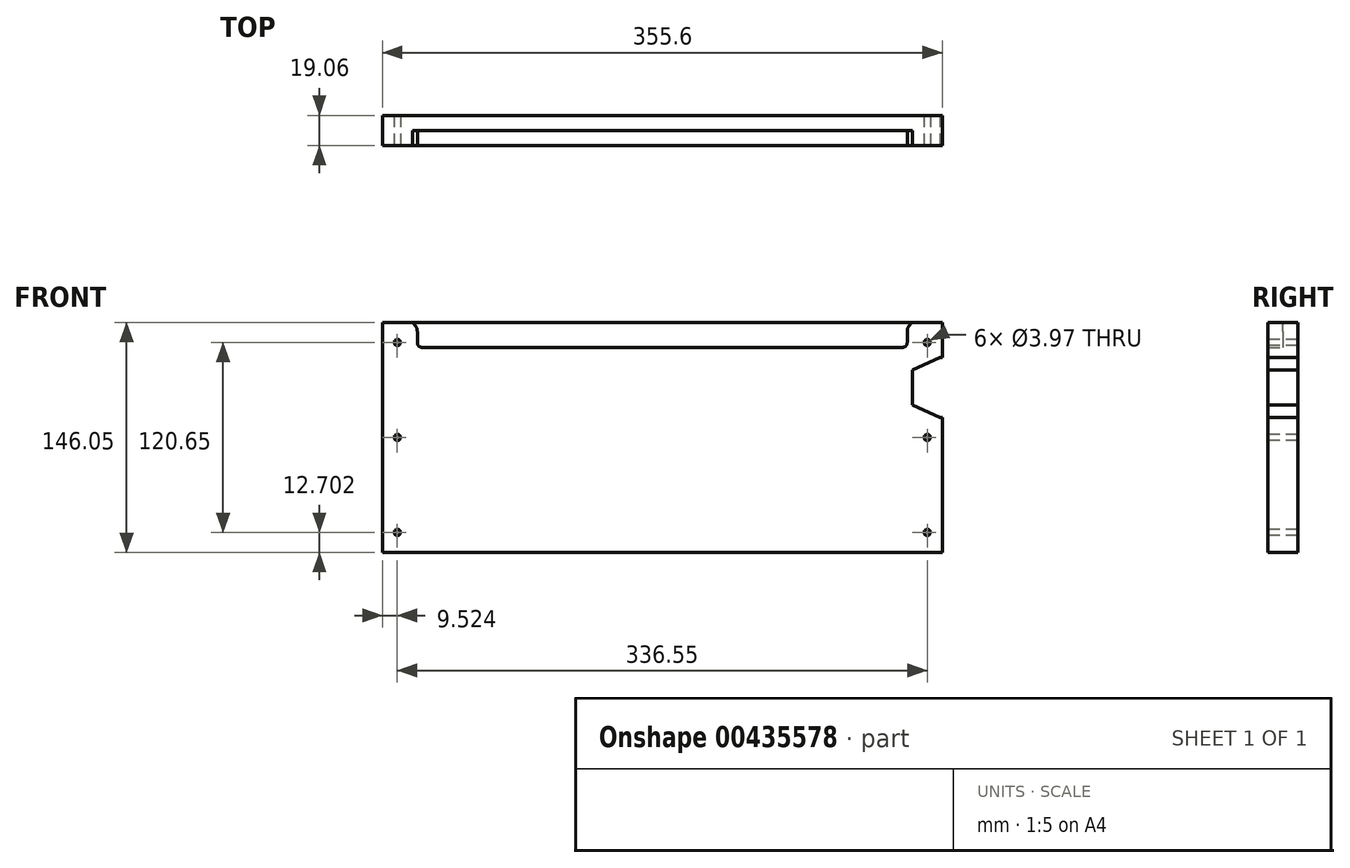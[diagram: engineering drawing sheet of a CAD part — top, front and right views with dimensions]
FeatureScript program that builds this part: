
annotation { "Feature Type Name" : "Feature", "Feature Type Description" : "" }
export const myFeature = defineFeature(function(context is Context, id is Id, definition is map)
    precondition{}
    {
        {
            var Q0;
            Q0=qCreatedBy(makeId("Front.planeOp"),FACE);
            var sketch = newSketch(context, id + "F0", { "sketchPlane" : qUnion([Q0])});
            skLineSegment(sketch, "E0", {"start": v(109.86, 42.77) * mm, "end": v(109.86, 55.47) * mm});
            skLineSegment(sketch, "E1", {"start": v(-198.11, 39.6) * mm, "end": v(106.69, 39.6) * mm});
            skLineSegment(sketch, "E2.bottom", {"start": v(-223.51, 55.47) * mm, "end": v(132.09, 55.47) * mm});
            skLineSegment(sketch, "E2.top", {"start": v(-223.51, -90.58) * mm, "end": v(132.09, -90.58) * mm});
            skLineSegment(sketch, "E2.right", {"start": v(132.09, 55.47) * mm, "end": v(132.09, -90.58) * mm});
            skLineSegment(sketch, "E3", {"start": v(-223.51, -17.55) * mm, "end": v(132.09, -17.55) * mm, "construction": true});
            skLineSegment(sketch, "E4", {"start": v(-45.71, 55.47) * mm, "end": v(-45.71, -90.58) * mm, "construction": true});
            skLineSegment(sketch, "E5", {"start": v(132.09, -30.25) * mm, "end": v(131.88, -30.25) * mm});
            skLineSegment(sketch, "E6", {"start": v(129.25, -30.82) * mm, "end": v(116.76, -36.5) * mm});
            skLineSegment(sketch, "E7", {"start": v(113.04, -42.28) * mm, "end": v(113.04, -56.33) * mm});
            skLineSegment(sketch, "E8", {"start": v(116.76, -62.1) * mm, "end": v(129.25, -67.78) * mm});
            skLineSegment(sketch, "E9", {"start": v(131.88, -68.35) * mm, "end": v(132.09, -68.35) * mm});
            skPoint(sketch, "E10.visualSharp", {"position": v(130.5, -30.25) * mm});
            skArc(sketch, "E10.filletArc", {"start": v(131.88, -30.25) * mm, "mid": v(130.53, -30.4) * mm, "end": v(129.25, -30.82) * mm});
            skPoint(sketch, "E11.visualSharp", {"position": v(113.04, -38.2) * mm});
            skArc(sketch, "E11.filletArc", {"start": v(116.76, -36.5) * mm, "mid": v(114.05, -38.84) * mm, "end": v(113.04, -42.28) * mm});
            skPoint(sketch, "E12.visualSharp", {"position": v(113.04, -60.42) * mm});
            skArc(sketch, "E12.filletArc", {"start": v(113.04, -56.33) * mm, "mid": v(114.05, -59.76) * mm, "end": v(116.76, -62.1) * mm});
            skPoint(sketch, "E13.visualSharp", {"position": v(130.5, -68.35) * mm});
            skArc(sketch, "E13.filletArc", {"start": v(129.25, -67.78) * mm, "mid": v(130.53, -68.2) * mm, "end": v(131.88, -68.35) * mm});
            skLineSegment(sketch, "E14.MirrorCS", {"start": v(-223.51, 55.47) * mm, "end": v(-223.51, -90.58) * mm});
            skArc(sketch, "E15.filletArc", {"start": v(-201.29, 42.77) * mm, "mid": v(-200.36, 40.53) * mm, "end": v(-198.11, 39.6) * mm});
            skArc(sketch, "E16.filletArc", {"start": v(106.69, 39.6) * mm, "mid": v(108.93, 40.53) * mm, "end": v(109.86, 42.77) * mm});
            skLineSegment(sketch, "E17.MirrorCS", {"start": v(131.88, 33.25) * mm, "end": v(132.09, 33.25) * mm});
            skLineSegment(sketch, "E18.MirrorCS", {"start": v(132.09, -4.85) * mm, "end": v(131.88, -4.85) * mm});
            skArc(sketch, "E19.MirrorCS", {"start": v(129.25, 32.68) * mm, "mid": v(130.53, 33.1) * mm, "end": v(131.88, 33.25) * mm});
            skArc(sketch, "E20.MirrorCS", {"start": v(131.88, -4.85) * mm, "mid": v(130.53, -4.7) * mm, "end": v(129.25, -4.28) * mm});
            skArc(sketch, "E21.MirrorCS", {"start": v(113.04, 21.22) * mm, "mid": v(114.05, 24.66) * mm, "end": v(116.76, 27) * mm});
            skLineSegment(sketch, "E22.MirrorCS", {"start": v(106.65, 22.4) * mm, "end": v(138.44, 36.85) * mm});
            skLineSegment(sketch, "E23.MirrorCS", {"start": v(138.44, -8.46) * mm, "end": v(106.65, 5.99) * mm});
            skLineSegment(sketch, "E24.MirrorCS", {"start": v(138.44, -4.85) * mm, "end": v(122.56, -4.85) * mm});
            skLineSegment(sketch, "E25.MirrorCS", {"start": v(122.56, 33.25) * mm, "end": v(138.44, 33.25) * mm});
            skArc(sketch, "E26.MirrorCS", {"start": v(116.76, 1.4) * mm, "mid": v(114.05, 3.74) * mm, "end": v(113.04, 7.17) * mm});
            skLineSegment(sketch, "E27.MirrorCS", {"start": v(129.25, -4.28) * mm, "end": v(116.76, 1.4) * mm});
            skLineSegment(sketch, "E28.MirrorCS", {"start": v(113.04, 7.17) * mm, "end": v(113.04, 21.22) * mm});
            skLineSegment(sketch, "E29.MirrorCS", {"start": v(116.76, 27) * mm, "end": v(129.25, 32.68) * mm});
            skLineSegment(sketch, "E30.MirrorCS", {"start": v(113.04, -1.68) * mm, "end": v(113.04, 36.42) * mm});
            skPoint(sketch, "E31.MirrorP", {"position": v(130.5, -4.85) * mm});
            skPoint(sketch, "E32.MirrorP", {"position": v(113.04, 25.3) * mm});
            skPoint(sketch, "E33.MirrorP", {"position": v(113.04, 3.08) * mm});
            skPoint(sketch, "E34.MirrorP", {"position": v(130.5, 33.25) * mm});
            skLineSegment(sketch, "E35.MirrorCS", {"start": v(-223.3, 33.25) * mm, "end": v(-223.51, 33.25) * mm});
            skLineSegment(sketch, "E36.MirrorCS", {"start": v(-223.51, -4.85) * mm, "end": v(-223.3, -4.85) * mm});
            skLineSegment(sketch, "E37.MirrorCS", {"start": v(-223.3, -68.35) * mm, "end": v(-223.51, -68.35) * mm});
            skArc(sketch, "E38.MirrorCS", {"start": v(-223.3, -30.25) * mm, "mid": v(-221.95, -30.4) * mm, "end": v(-220.67, -30.82) * mm});
            skArc(sketch, "E39.MirrorCS", {"start": v(-220.67, 32.68) * mm, "mid": v(-221.95, 33.1) * mm, "end": v(-223.3, 33.25) * mm});
            skArc(sketch, "E40.MirrorCS", {"start": v(-223.3, -4.85) * mm, "mid": v(-221.95, -4.7) * mm, "end": v(-220.67, -4.28) * mm});
            skArc(sketch, "E41.MirrorCS", {"start": v(-220.67, -67.78) * mm, "mid": v(-221.95, -68.2) * mm, "end": v(-223.3, -68.35) * mm});
            skLineSegment(sketch, "E42.MirrorCS", {"start": v(-223.51, -30.25) * mm, "end": v(-223.3, -30.25) * mm});
            skArc(sketch, "E43.MirrorCS", {"start": v(-208.18, -36.5) * mm, "mid": v(-205.47, -38.84) * mm, "end": v(-204.46, -42.28) * mm});
            skLineSegment(sketch, "E44.MirrorCS", {"start": v(-220.67, -4.28) * mm, "end": v(-208.18, 1.4) * mm});
            skArc(sketch, "E45.MirrorCS", {"start": v(-208.18, 1.4) * mm, "mid": v(-205.47, 3.74) * mm, "end": v(-204.46, 7.17) * mm});
            skArc(sketch, "E46.MirrorCS", {"start": v(-204.46, -56.33) * mm, "mid": v(-205.47, -59.76) * mm, "end": v(-208.18, -62.1) * mm});
            skArc(sketch, "E47.MirrorCS", {"start": v(-204.46, 21.22) * mm, "mid": v(-205.47, 24.66) * mm, "end": v(-208.18, 27) * mm});
            skLineSegment(sketch, "E48.MirrorCS", {"start": v(-220.67, -30.82) * mm, "end": v(-208.18, -36.5) * mm});
            skLineSegment(sketch, "E49.MirrorCS", {"start": v(-208.18, 27) * mm, "end": v(-220.67, 32.68) * mm});
            skLineSegment(sketch, "E50.MirrorCS", {"start": v(-208.18, -62.1) * mm, "end": v(-220.67, -67.78) * mm});
            skPoint(sketch, "E51.MirrorP", {"position": v(-204.46, 3.08) * mm});
            skPoint(sketch, "E52.MirrorP", {"position": v(-204.46, -38.2) * mm});
            skPoint(sketch, "E53.MirrorP", {"position": v(-221.92, 33.25) * mm});
            skPoint(sketch, "E54.MirrorP", {"position": v(-204.46, 25.3) * mm});
            skLineSegment(sketch, "E55.MirrorCS", {"start": v(-204.46, 7.17) * mm, "end": v(-204.46, 21.22) * mm});
            skPoint(sketch, "E56.MirrorP", {"position": v(-221.92, -68.35) * mm});
            skPoint(sketch, "E57.MirrorP", {"position": v(-204.46, -60.42) * mm});
            skLineSegment(sketch, "E58.MirrorCS", {"start": v(-204.46, -42.28) * mm, "end": v(-204.46, -56.33) * mm});
            skPoint(sketch, "E59.MirrorP", {"position": v(-221.92, -30.25) * mm});
            skPoint(sketch, "E60.MirrorP", {"position": v(-221.92, -4.85) * mm});
            skCircle(sketch, "E61", {"center": v(122.56, -77.88) * mm, "radius": 1.98 * mm});
            skCircle(sketch, "E62", {"center": v(122.56, -17.55) * mm, "radius": 1.98 * mm});
            skCircle(sketch, "E63.MirrorC", {"center": v(122.56, 42.77) * mm, "radius": 1.98 * mm});
            skCircle(sketch, "E64.MirrorC", {"center": v(-213.99, -77.88) * mm, "radius": 1.98 * mm});
            skCircle(sketch, "E65.MirrorC", {"center": v(-213.99, -17.55) * mm, "radius": 1.98 * mm});
            skCircle(sketch, "E66.MirrorC", {"center": v(-213.99, 42.77) * mm, "radius": 1.98 * mm});
            skLineSegment(sketch, "E67", {"start": v(-201.29, 55.47) * mm, "end": v(-201.29, 42.77) * mm});
            skSolve(sketch);
        }
        {
            var Q0;
            {var subQ22=sQuery(id+"F0.wireOp",EDGE,"E0");Q0=makeQuery(id+"F0.imprint","IMPRINT",FACE,{"disambiguationData":[TD([[makeQuery(id+"F0.imprint","IMPRINT",EDGE,{"derivedFrom":subQ22}),-1.0]])]});}
            var Q1;
            {var subQ1=sQuery(id+"F0.wireOp",EDGE,"E0");Q1=makeQuery(id+"F0.imprint","IMPRINT",FACE,{"disambiguationData":[TD([[makeQuery(id+"F0.imprint","IMPRINT",EDGE,{"derivedFrom":subQ1}),1.0]])]});}
            var Q2;
            {var subQ0=sQuery(id+"F0.wireOp",EDGE,"E24.MirrorCS");var subQ1=sQuery(id+"F0.wireOp",EDGE,"E2.right");var subQ2=makeQuery(id+"F0.imprint","INTERSECT",VERTEX,{"derivedFrom":[subQ1,subQ0]});Q2=makeQuery(id+"F0.imprint","IMPRINT",FACE,{"disambiguationData":[TD([[makeQuery(id+"F0.imprint","IMPRINT",EDGE,{"disambiguationData":[TD([[subQ2,-1.0]])],"derivedFrom":subQ1}),-1.0]])]});}
            var Q3;
            {var subQ0=sQuery(id+"F0.wireOp",EDGE,"E22.MirrorCS");var subQ1=sQuery(id+"F0.wireOp",EDGE,"E2.right");var subQ2=makeQuery(id+"F0.imprint","INTERSECT",VERTEX,{"derivedFrom":[subQ1,subQ0]});Q3=makeQuery(id+"F0.imprint","IMPRINT",FACE,{"disambiguationData":[TD([[makeQuery(id+"F0.imprint","IMPRINT",EDGE,{"disambiguationData":[TD([[subQ2,-1.0]])],"derivedFrom":subQ1}),-1.0]])]});}
            extrude(context, id + "F1", {"entities" : qUnion([Q0, Q1, Q2, Q3]), "oppositeDirection" : true, "depth" : 9.52 * mm, "offsetDistance" : 25.4 * mm});
        }
        {
            var Q0;
            {var subQ22=sQuery(id+"F0.wireOp",EDGE,"E0");Q0=makeQuery(id+"F0.imprint","IMPRINT",FACE,{"disambiguationData":[TD([[makeQuery(id+"F0.imprint","IMPRINT",EDGE,{"derivedFrom":subQ22}),-1.0]])]});}
            var Q1;
            {var subQ0=sQuery(id+"F0.wireOp",EDGE,"E22.MirrorCS");var subQ1=sQuery(id+"F0.wireOp",EDGE,"E2.right");var subQ2=makeQuery(id+"F0.imprint","INTERSECT",VERTEX,{"derivedFrom":[subQ1,subQ0]});Q1=makeQuery(id+"F0.imprint","IMPRINT",FACE,{"disambiguationData":[TD([[makeQuery(id+"F0.imprint","IMPRINT",EDGE,{"disambiguationData":[TD([[subQ2,-1.0]])],"derivedFrom":subQ1}),-1.0]])]});}
            var Q2;
            {var subQ0=sQuery(id+"F0.wireOp",EDGE,"E24.MirrorCS");var subQ1=sQuery(id+"F0.wireOp",EDGE,"E2.right");var subQ2=makeQuery(id+"F0.imprint","INTERSECT",VERTEX,{"derivedFrom":[subQ1,subQ0]});Q2=makeQuery(id+"F0.imprint","IMPRINT",FACE,{"disambiguationData":[TD([[makeQuery(id+"F0.imprint","IMPRINT",EDGE,{"disambiguationData":[TD([[subQ2,-1.0]])],"derivedFrom":subQ1}),-1.0]])]});}
            extrude(context, id + "F2", {"entities" : qUnion([Q0, Q1, Q2]), "operationType" : NewBodyOperationType.ADD, "depth" : 9.52 * mm, "offsetDistance" : 25.4 * mm});
        }
        {
            var Q0;
            Q0=makeQuery(id+"F2.opExtrude","SWEPT_EDGE",EDGE,{"disambiguationData":[OSD([sQuery(id+"F0.wireOp",EDGE,"E2.bottom"),sQuery(id+"F0.wireOp",EDGE,"E67")])]});
            var Q1;
            Q1=makeQuery(id+"F2.opExtrude","SWEPT_EDGE",EDGE,{"disambiguationData":[OSD([sQuery(id+"F0.wireOp",EDGE,"E0"),sQuery(id+"F0.wireOp",EDGE,"E2.bottom")])]});
            chamfer(context, id + "F3", {"entities" : qUnion([Q0, Q1]), "width" : 3.17 * mm, "tangentPropagation" : true});
        }
        {
            var Q0;
            {var subQ0=sQuery(id+"F0.wireOp",EDGE,"E0");Q0=makeQuery(id+"F3.opChamfer","BLEND_EDGE",EDGE,{"blendedFrom":[makeQuery(id+"F2.opExtrude","SWEPT_EDGE",EDGE,{"disambiguationData":[OSD([subQ0,sQuery(id+"F0.wireOp",EDGE,"E2.bottom")])]}),makeQuery(id+"F2.opExtrude","SWEPT_FACE",FACE,{"disambiguationData":[OSD([subQ0])]})],"blendedInto":[makeQuery(id+"F2.opExtrude","SWEPT_FACE",FACE,{"disambiguationData":[OSD([subQ0])]})]});}
            var Q1;
            {var subQ0=sQuery(id+"F0.wireOp",EDGE,"E67");Q1=makeQuery(id+"F3.opChamfer","BLEND_EDGE",EDGE,{"blendedFrom":[makeQuery(id+"F2.opExtrude","SWEPT_EDGE",EDGE,{"disambiguationData":[OSD([sQuery(id+"F0.wireOp",EDGE,"E2.bottom"),subQ0])]}),makeQuery(id+"F2.opExtrude","SWEPT_FACE",FACE,{"disambiguationData":[OSD([subQ0])]})],"blendedInto":[makeQuery(id+"F2.opExtrude","SWEPT_FACE",FACE,{"disambiguationData":[OSD([subQ0])]})]});}
            fillet(context, id + "F4", {"entities" : qUnion([Q0, Q1]), "radius" : 6.35 * mm, "tangentPropagation" : true, "allowEdgeOverflow" : false});
        }
    });
